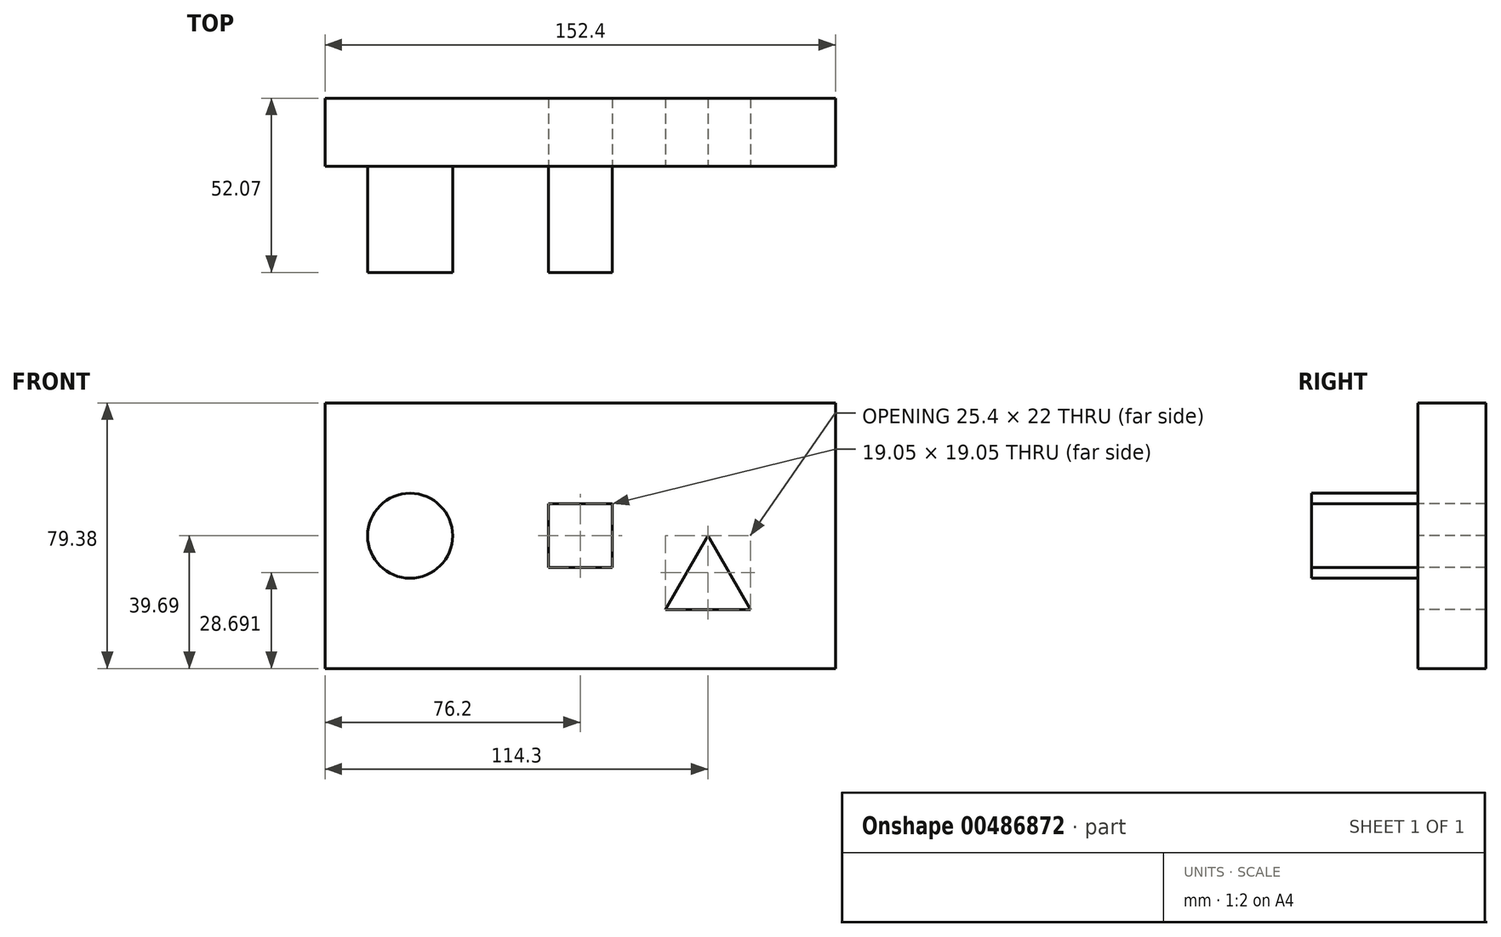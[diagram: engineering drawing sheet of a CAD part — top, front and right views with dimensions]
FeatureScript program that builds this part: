
annotation { "Feature Type Name" : "Feature", "Feature Type Description" : "" }
export const myFeature = defineFeature(function(context is Context, id is Id, definition is map)
    precondition{}
    {
        {
            var Q0;
            Q0=qCreatedBy(makeId("Front.planeOp"),FACE);
            var sketch = newSketch(context, id + "F0", { "sketchPlane" : qUnion([Q0])});
            skLineSegment(sketch, "E0.bottom", {"start": v(76.2, -39.69) * mm, "end": v(-76.2, -39.69) * mm});
            skLineSegment(sketch, "E0.top", {"start": v(76.2, 39.69) * mm, "end": v(-76.2, 39.69) * mm});
            skLineSegment(sketch, "E0.left", {"start": v(76.2, -39.69) * mm, "end": v(76.2, 39.69) * mm});
            skLineSegment(sketch, "E0.right", {"start": v(-76.2, -39.69) * mm, "end": v(-76.2, 39.69) * mm});
            skPoint(sketch, "E0.middle", {"position": v(0, 0) * mm});
            skLineSegment(sketch, "E1.bottom", {"start": v(9.53, -9.52) * mm, "end": v(-9.52, -9.53) * mm});
            skLineSegment(sketch, "E1.top", {"start": v(9.52, 9.53) * mm, "end": v(-9.53, 9.52) * mm});
            skLineSegment(sketch, "E1.left", {"start": v(9.53, -9.52) * mm, "end": v(9.52, 9.53) * mm});
            skLineSegment(sketch, "E1.right", {"start": v(-9.52, -9.53) * mm, "end": v(-9.53, 9.52) * mm});
            skLineSegment(sketch, "E2", {"start": v(0, 0) * mm, "end": v(-50.8, 0) * mm});
            skPoint(sketch, "E2.endSnap0", {"position": v(-9.53, 0) * mm});
            skCircle(sketch, "E3", {"center": v(-50.8, 0) * mm, "radius": 12.7 * mm});
            skLineSegment(sketch, "E4", {"start": v(0, 0) * mm, "end": v(38.1, 0) * mm});
            skLineSegment(sketch, "E5", {"start": v(38.1, 0) * mm, "end": v(25.4, -22) * mm});
            skLineSegment(sketch, "E6", {"start": v(25.4, -22) * mm, "end": v(50.8, -22) * mm});
            skLineSegment(sketch, "E7", {"start": v(50.8, -22) * mm, "end": v(38.1, 0) * mm});
            skSolve(sketch);
        }
        {
            var Q0;
            Q0=makeQuery(id+"F0.imprint","IMPRINT",FACE,{"disambiguationData":[TD([[makeQuery(id+"F0.imprint","IMPRINT",EDGE,{"derivedFrom":sQuery(id+"F0.wireOp",EDGE,"E0.bottom")}),-1.0]])]});
            extrude(context, id + "F1", {"entities" : qUnion([Q0]), "oppositeDirection" : true, "depth" : 20.32 * mm});
        }
        {
            var Q0;
            {var subQ1=sQuery(id+"F0.wireOp",EDGE,"E1.top");Q0=makeQuery(id+"F0.imprint","IMPRINT",FACE,{"disambiguationData":[TD([[makeQuery(id+"F0.imprint","IMPRINT",EDGE,{"derivedFrom":subQ1}),1.0]])]});}
            var Q1;
            {var subQ5=sQuery(id+"F0.wireOp",EDGE,"E1.bottom");Q1=makeQuery(id+"F0.imprint","IMPRINT",FACE,{"disambiguationData":[TD([[makeQuery(id+"F0.imprint","IMPRINT",EDGE,{"derivedFrom":subQ5}),-1.0]])]});}
            extrude(context, id + "F2", {"entities" : qUnion([Q0, Q1]), "depth" : 31.75 * mm});
        }
        {
            var Q0;
            Q0=makeQuery(id+"F0.imprint","IMPRINT",FACE,{"disambiguationData":[TD([[makeQuery(id+"F0.imprint","IMPRINT",EDGE,{"derivedFrom":sQuery(id+"F0.wireOp",EDGE,"E3")}),1.0]])]});
            extrude(context, id + "F3", {"entities" : qUnion([Q0]), "operationType" : NewBodyOperationType.ADD, "oppositeDirection" : true, "depth" : 20.32 * mm, "hasSecondDirection" : true, "secondDirectionOppositeDirection" : false, "secondDirectionDepth" : 31.75 * mm});
        }
    });
